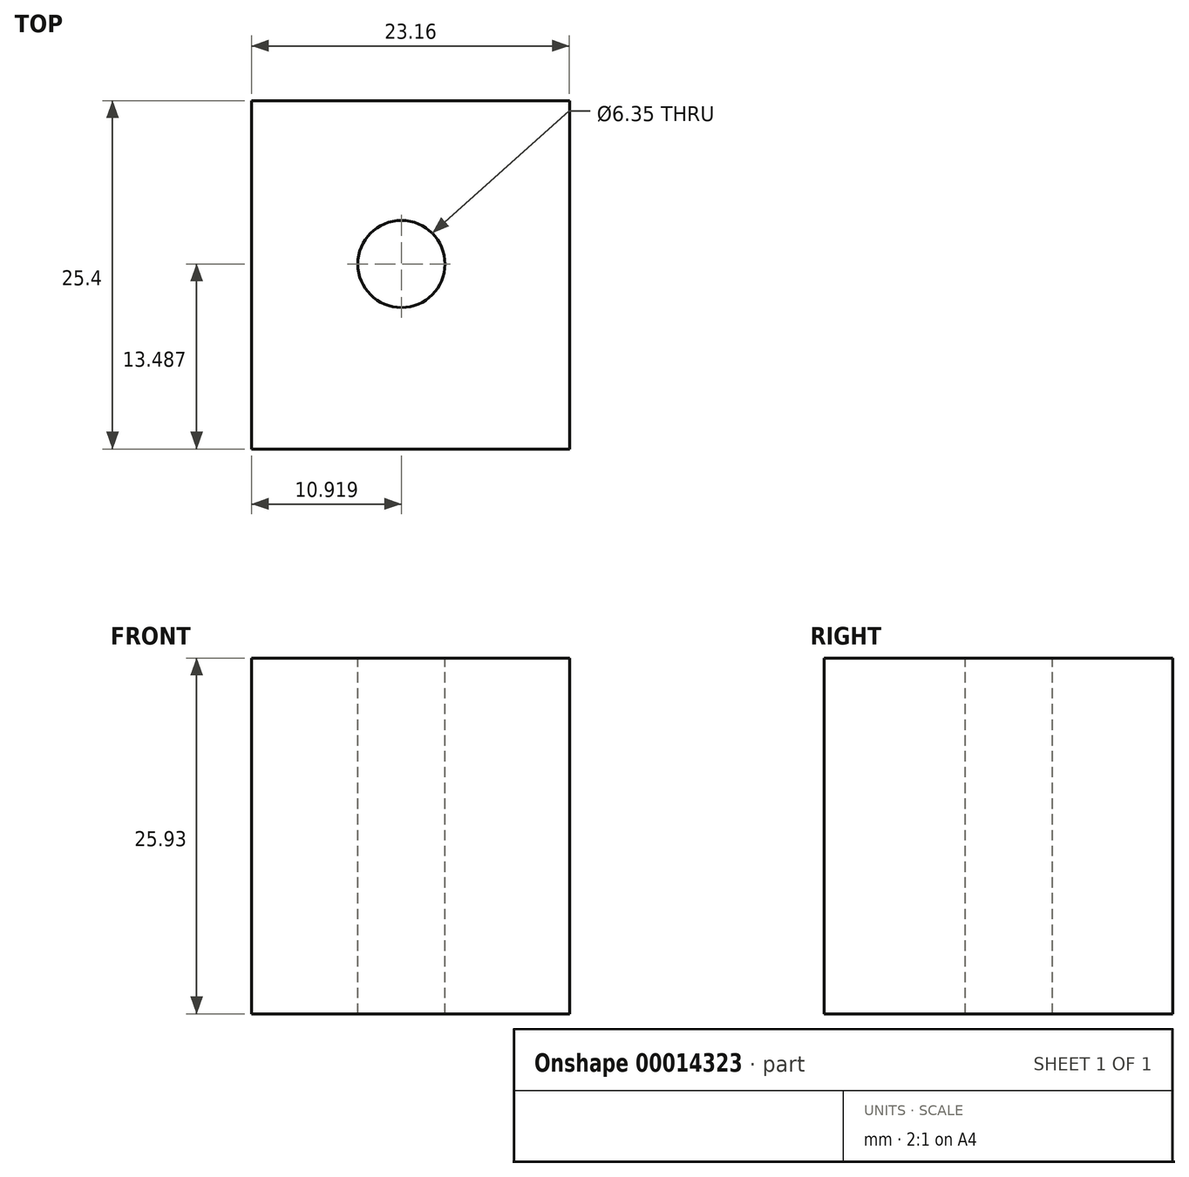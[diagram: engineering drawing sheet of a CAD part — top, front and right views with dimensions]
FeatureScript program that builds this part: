
annotation { "Feature Type Name" : "Feature", "Feature Type Description" : "" }
export const myFeature = defineFeature(function(context is Context, id is Id, definition is map)
    precondition{}
    {
        {
            var Q0;
            Q0=qCreatedBy(makeId("Front.planeOp"),FACE);
            var sketch = newSketch(context, id + "F0", { "sketchPlane" : qUnion([Q0])});
            skLineSegment(sketch, "E0.bottom", {"start": v(31.1, -9.16) * mm, "end": v(7.93, -9.16) * mm});
            skLineSegment(sketch, "E0.top", {"start": v(31.1, 16.77) * mm, "end": v(7.93, 16.77) * mm});
            skLineSegment(sketch, "E0.left", {"start": v(31.1, -9.16) * mm, "end": v(31.1, 16.77) * mm});
            skLineSegment(sketch, "E0.right", {"start": v(7.93, -9.16) * mm, "end": v(7.93, 16.77) * mm});
            skSolve(sketch);
        }
        {
            var Q0;
            Q0 = qSketchRegion(id + "F0", true);
            extrude(context, id + "F1", {"entities" : qUnion([Q0]), "depth" : 25.4 * mm});
        }
        {
            var Q0;
            Q0=makeQuery(id+"F1.opExtrude","SWEPT_FACE",FACE,{"disambiguationData":[OSD([sQuery(id+"F0.wireOp",EDGE,"E0.top")])]});
            var sketch = newSketch(context, id + "F2", { "sketchPlane" : qUnion([Q0])});
            skPoint(sketch, "E1", {"position": v(18.85, -11.91) * mm});
            skSolve(sketch);
        }
        {
            var Q0;
            Q0=sQuery(id+"F2.wireOp",VERTEX,"E1");
            var Q1;
            Q1=makeQuery(id+"F1.opExtrude","SWEPT_BODY",BODY,{"disambiguationData":[OSD([sQuery(id+"F0.wireOp",EDGE,"E0.bottom"),sQuery(id+"F0.wireOp",EDGE,"E0.top"),sQuery(id+"F0.wireOp",EDGE,"E0.left"),sQuery(id+"F0.wireOp",EDGE,"E0.right")])]});
            hole(context, id + "F3", {"style" : HoleStyle.SIMPLE, "holeDiameter" : 6.35 * mm, "endStyle" : HoleEndStyle.THROUGH, "locations" : qUnion([Q0]), "scope" : qUnion([Q1])});
        }
    });
